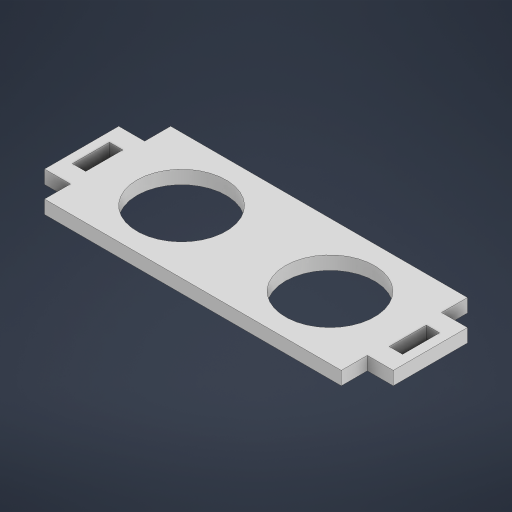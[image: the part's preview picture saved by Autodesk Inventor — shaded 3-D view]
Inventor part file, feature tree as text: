
AUTODESK INVENTOR PART (.ipt)
format: ipt  version: 2024 (Build 280153000, 153)  size: 205,824 bytes
history: native  units: mm
features: other x1, extrude x1, sketch x1
ambient origin geometry x8: Origin, YZ Plane, XZ Plane, XY Plane, X Axis, Y Axis, Z Axis, Center Point
bodies: Body1 (feature_tree)
feature tree (3):
  other  "Sólido1"
  extrude  "Extrusión1"  Depth=18.0mm
  sketch  "Boceto1"  dims[d4=120.0mm d5=18.0mm d6=35.0mm d7=35.0mm d8=35.0mm d9=50.0mm d10=25.0mm d11=12.5mm d12=100.0mm d13=18.0mm d14=0.0mm d15=470.0mm d16=12.5mm d17=18.0mm]
